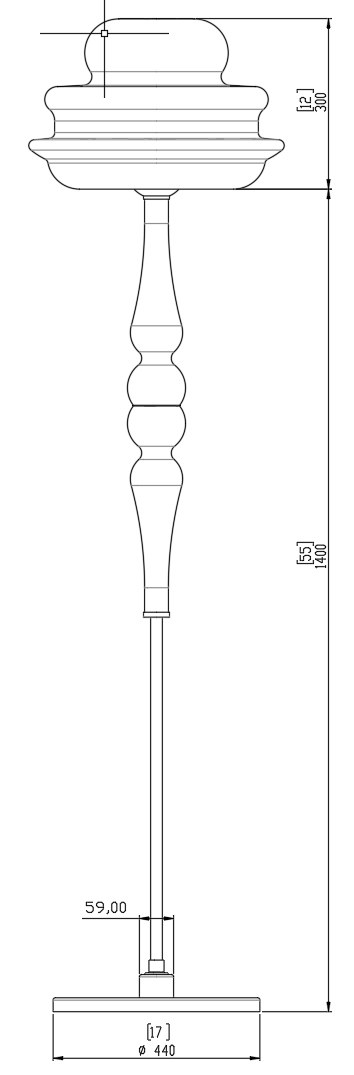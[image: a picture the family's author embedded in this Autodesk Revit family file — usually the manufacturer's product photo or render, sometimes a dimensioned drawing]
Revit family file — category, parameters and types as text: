
# Revit family: NOVECENTO-Table
name_source: partatom
category: Lighting Fixtures
units: mm (PartAtom-declared; Revit-internal decimal feet)

## family parameters
Always vertical = Yes
Cut with Voids When Loaded = No
Light Source = No
OmniClass Number = 23.80.70.00
OmniClass Title = Lighting
Part Type = Normal
Room Calculation Point = No
Round Connector Dimension = Use Diameter
Shared = No
Work Plane-Based = Yes

## types (1)
- NOVECENTO LT
    Bulb Diametr = 15 mm  [stored 0.0492126 ft]
    Country = Europe
    Default Elevation = 1219 mm
    Depth = 41 mm
    Description = TABLE LAMP
    Designer = Studio Debonademeo
    Manufacturer = Vistosi
    Manufacturer country = Italy
    Model = NOVECENTO
    Type Comments = Studio Debonademeo
    URL = https://vistosi.com
    URL Product Page = https://vistosi.it
    Width = 54 mm

note: [stored X ft] marks values corroborated as IEEE doubles in the binary element streams (Revit-internal decimal feet)

## geometry (parser evidence)
native form markers: Sweep x9
no freeform markers — native parametric forms only
